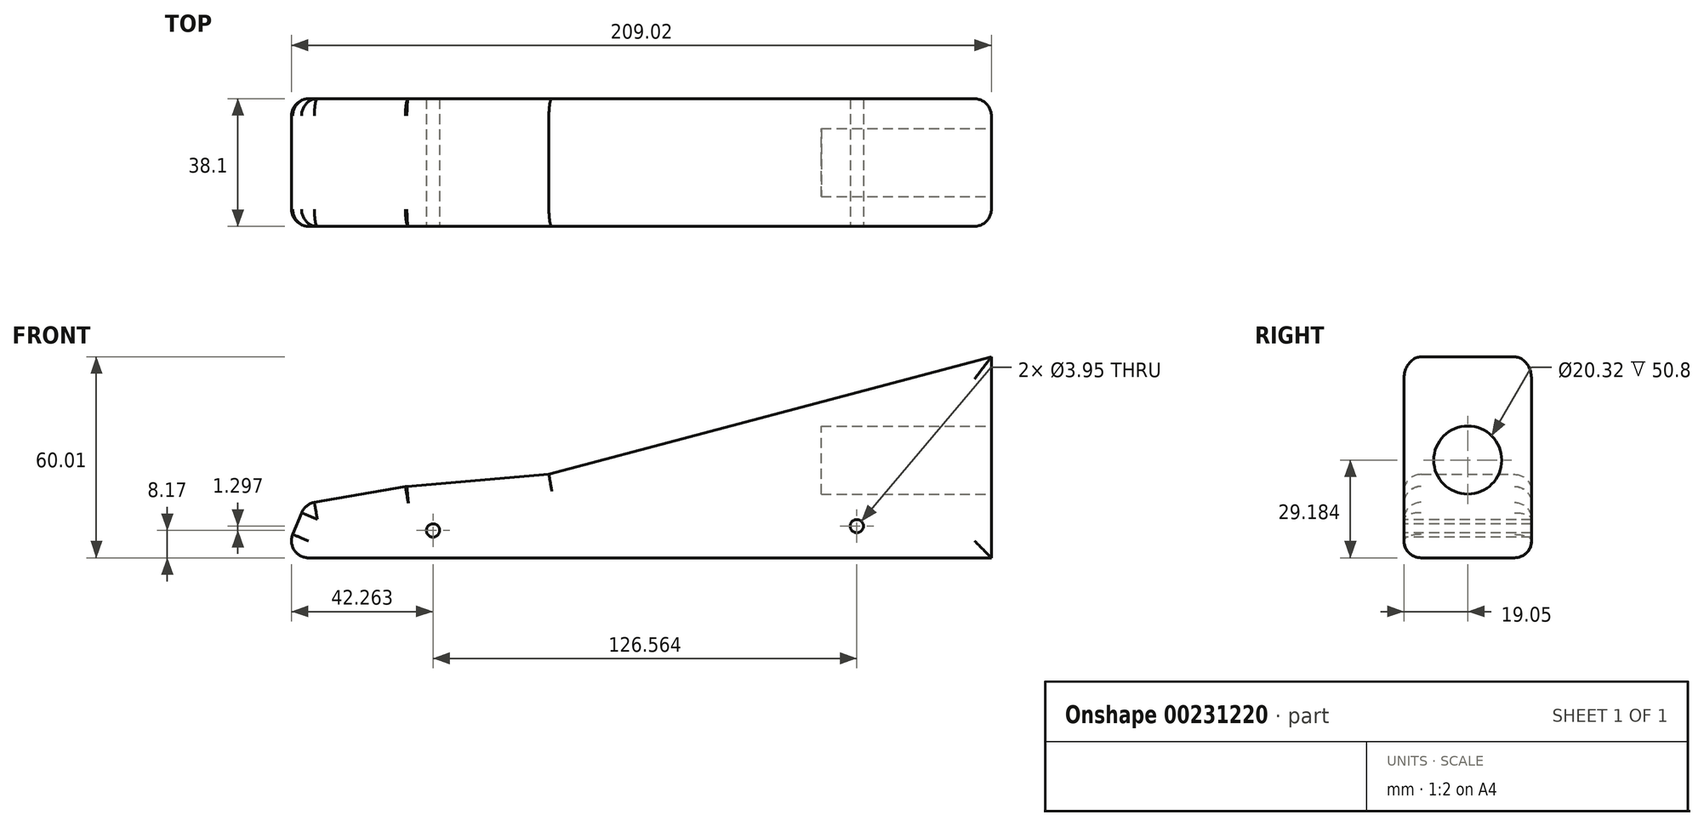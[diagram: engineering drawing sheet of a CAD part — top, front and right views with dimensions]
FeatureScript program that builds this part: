
annotation { "Feature Type Name" : "Feature", "Feature Type Description" : "" }
export const myFeature = defineFeature(function(context is Context, id is Id, definition is map)
    precondition{}
    {
        {
            var Q0;
            Q0=qCreatedBy(makeId("Front.planeOp"),FACE);
            var sketch = newSketch(context, id + "F0", { "sketchPlane" : qUnion([Q0])});
            skLineSegment(sketch, "E0", {"start": v(-104.28, 0) * mm, "end": v(107.23, 0) * mm});
            skLineSegment(sketch, "E1", {"start": v(107.23, 0) * mm, "end": v(107.23, 60) * mm});
            skLineSegment(sketch, "E2", {"start": v(107.23, 60) * mm, "end": v(-24.92, 24.92) * mm});
            skLineSegment(sketch, "E3", {"start": v(-24.92, 24.92) * mm, "end": v(-67.55, 21.31) * mm});
            skLineSegment(sketch, "E4", {"start": v(-67.55, 21.31) * mm, "end": v(-97.72, 16.07) * mm});
            skLineSegment(sketch, "E5", {"start": v(-97.72, 16.07) * mm, "end": v(-104.28, 0) * mm});
            skSolve(sketch);
        }
        {
            var Q0;
            Q0=makeQuery(id+"F0.imprint","IMPRINT",FACE,{"disambiguationData":[TD([[makeQuery(id+"F0.imprint","IMPRINT",EDGE,{"derivedFrom":sQuery(id+"F0.wireOp",EDGE,"E0")}),1.0]])]});
            extrude(context, id + "F1", {"entities" : qUnion([Q0]), "depth" : 38.1 * mm});
        }
        {
            var Q0;
            Q0=makeQuery(id+"F1.opExtrude","CAP_FACE",FACE,{"disambiguationData":[OSD([sQuery(id+"F0.wireOp",EDGE,"E0"),sQuery(id+"F0.wireOp",EDGE,"E1"),sQuery(id+"F0.wireOp",EDGE,"E2"),sQuery(id+"F0.wireOp",EDGE,"E3"),sQuery(id+"F0.wireOp",EDGE,"E4"),sQuery(id+"F0.wireOp",EDGE,"E5")])],"isStart":false});
            fillet(context, id + "F2", {"entities" : qUnion([Q0]), "radius" : 5.08 * mm, "tangentPropagation" : true, "allowEdgeOverflow" : false});
        }
        {
            var Q0;
            Q0=makeQuery(id+"F1.opExtrude","CAP_FACE",FACE,{"disambiguationData":[OSD([sQuery(id+"F0.wireOp",EDGE,"E0"),sQuery(id+"F0.wireOp",EDGE,"E1"),sQuery(id+"F0.wireOp",EDGE,"E2"),sQuery(id+"F0.wireOp",EDGE,"E3"),sQuery(id+"F0.wireOp",EDGE,"E4"),sQuery(id+"F0.wireOp",EDGE,"E5")])],"isStart":true});
            fillet(context, id + "F3", {"entities" : qUnion([Q0]), "radius" : 5.08 * mm, "tangentPropagation" : true, "allowEdgeOverflow" : false});
        }
        {
            var Q0;
            Q0=makeQuery(id+"F1.opExtrude","SWEPT_FACE",FACE,{"disambiguationData":[OSD([sQuery(id+"F0.wireOp",EDGE,"E5")])]});
            fillet(context, id + "F4", {"entities" : qUnion([Q0]), "radius" : 5.08 * mm, "tangentPropagation" : true, "allowEdgeOverflow" : false});
        }
        {
            var Q0;
            Q0=makeQuery(id+"F1.opExtrude","SWEPT_FACE",FACE,{"disambiguationData":[OSD([sQuery(id+"F0.wireOp",EDGE,"E4")])]});
            fillet(context, id + "F5", {"entities" : qUnion([Q0]), "radius" : 5.08 * mm, "tangentPropagation" : true, "allowEdgeOverflow" : false});
        }
        {
            var Q0;
            Q0=makeQuery(id+"F1.opExtrude","SWEPT_FACE",FACE,{"disambiguationData":[OSD([sQuery(id+"F0.wireOp",EDGE,"E1")])]});
            var sketch = newSketch(context, id + "F6", { "sketchPlane" : qUnion([Q0])});
            skCircle(sketch, "E6", {"center": v(-19.05, 29.18) * mm, "radius": 10.16 * mm});
            skSolve(sketch);
        }
        {
            var Q0;
            Q0=makeQuery(id+"F6.imprint","IMPRINT",FACE,{"disambiguationData":[TD([[makeQuery(id+"F6.imprint","IMPRINT",EDGE,{"derivedFrom":sQuery(id+"F6.wireOp",EDGE,"E6")}),1.0]])]});
            extrude(context, id + "F7", {"entities" : qUnion([Q0]), "operationType" : NewBodyOperationType.REMOVE, "oppositeDirection" : true, "depth" : 50.8 * mm});
        }
        {
            var Q0;
            Q0=makeQuery(id+"F1.opExtrude","CAP_FACE",FACE,{"disambiguationData":[OSD([sQuery(id+"F0.wireOp",EDGE,"E0"),sQuery(id+"F0.wireOp",EDGE,"E1"),sQuery(id+"F0.wireOp",EDGE,"E2"),sQuery(id+"F0.wireOp",EDGE,"E3"),sQuery(id+"F0.wireOp",EDGE,"E4"),sQuery(id+"F0.wireOp",EDGE,"E5")])],"isStart":false});
            var sketch = newSketch(context, id + "F8", { "sketchPlane" : qUnion([Q0])});
            skCircle(sketch, "E7", {"center": v(-59.53, 8.17) * mm, "radius": 1.98 * mm});
            skCircle(sketch, "E8", {"center": v(66.78, 8.95) * mm, "radius": 1.98 * mm});
            skSolve(sketch);
        }
        {
            var Q0;
            Q0=makeQuery(id+"F8.imprint","IMPRINT",FACE,{"disambiguationData":[TD([[makeQuery(id+"F8.imprint","IMPRINT",EDGE,{"derivedFrom":sQuery(id+"F8.wireOp",EDGE,"E7")}),1.0]])]});
            var Q1;
            Q1=sQuery(id+"F8.wireOp",EDGE,"E7");
            extrude(context, id + "F9", {"entities" : qUnion([Q0]), "operationType" : NewBodyOperationType.REMOVE, "surfaceEntities" : qUnion([Q1]), "oppositeDirection" : true, "depth" : 50.8 * mm});
        }
        {
            var Q0;
            Q0=makeQuery(id+"F1.opExtrude","CAP_FACE",FACE,{"disambiguationData":[OSD([sQuery(id+"F0.wireOp",EDGE,"E0"),sQuery(id+"F0.wireOp",EDGE,"E1"),sQuery(id+"F0.wireOp",EDGE,"E2"),sQuery(id+"F0.wireOp",EDGE,"E3"),sQuery(id+"F0.wireOp",EDGE,"E4"),sQuery(id+"F0.wireOp",EDGE,"E5")])],"isStart":false});
            var sketch = newSketch(context, id + "F10", { "sketchPlane" : qUnion([Q0])});
            skCircle(sketch, "E9", {"center": v(67.04, 9.47) * mm, "radius": 1.98 * mm});
            skSolve(sketch);
        }
        {
            var Q0;
            Q0=makeQuery(id+"F10.imprint","IMPRINT",FACE,{"disambiguationData":[TD([[makeQuery(id+"F10.imprint","IMPRINT",EDGE,{"derivedFrom":sQuery(id+"F10.wireOp",EDGE,"E9")}),1.0]])]});
            extrude(context, id + "F11", {"entities" : qUnion([Q0]), "operationType" : NewBodyOperationType.REMOVE, "oppositeDirection" : true, "depth" : 50.8 * mm});
        }
    });
